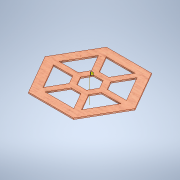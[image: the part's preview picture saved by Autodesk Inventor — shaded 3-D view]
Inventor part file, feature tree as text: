
AUTODESK INVENTOR PART (.ipt)
format: ipt  version: 2020 (Build 240168000, 168)  size: 286,208 bytes
history: native  units: mm
features: sketch x2, extrude x2
ambient origin geometry x8: Origin, YZ Plane, XZ Plane, XY Plane, X Axis, Y Axis, Z Axis, Center Point
bodies: Body1 (feature_tree)
feature tree (4):
  sketch  "Sketch6"  dims[d72=6.5mm d85=2.0mm d86=0.0mm]
  extrude  "Fronte"  Depth=2.0mm TaperAngle=0.0deg
  extrude  "Extrusion17"  Depth=2.0mm
  sketch  "Sketch11"  dims[d87=15.0mm d88=6.5mm d91=2.5mm d92=2.5mm d95=1.25mm d96=25.0mm d97=2.5mm d98=25.0mm d99=135.0deg d100=0.0mm d114=1.7mm d117=3.0mm d121=3.0mm d123=6.0mm d127=140.0mm d128=5.196152mm d129=5.196152mm d130=3.0mm d158=110.0mm d159=50.0mm d160=30.0mm d162=60.0mm d164=360.0deg d166=2.0mm d167=0.0mm]
